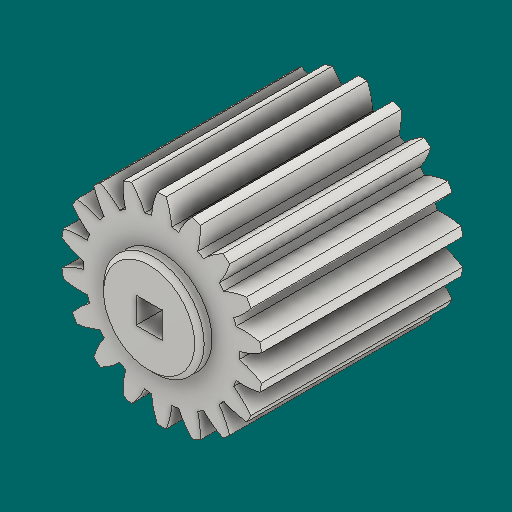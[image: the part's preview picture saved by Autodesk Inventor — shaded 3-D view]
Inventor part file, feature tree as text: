
AUTODESK INVENTOR PART (.ipt)
format: ipt  version: 2023.1 (Build 271208000, 208)  size: 353,792 bytes
history: native  units: in
note: dims shown in document units (in); Inventor stores cm internally (conversion verified against a paired STEP export)
features: other x12, sketch x5, plane x3
ambient origin geometry x8: Origin, YZ Plane, XZ Plane, XY Plane, X Axis, Y Axis, Z Axis, Center Point
bodies: Solid1 (feature_tree)
feature tree (20):
  other  "Spur Gear14_MIR.ipt"
  other  "Solid1::Spur Gear14_MIR.ipt"
  other  "TaggingFeature1"
  sketch  "Sketch1"  dims[d0=0.3937in]
  sketch  "Sketch2"  dims[d9=0.0in]
  sketch  "Sketch3"  dims[d14=0.0in]
  sketch  "Sketch4"  dims[d15=0.9in]
  sketch  "Sketch5"  dims[d16=0.0in d17=0.0in d18=0.0in d19=0.9in]
  plane  "XZ Plane_1"
  plane  "Work Plane2"
  plane  "Work Plane3"
  other  "Srf1"
  other  "Srf1::Derived"
  other  "Start plane iMate"
  other  "Distance iMate"
  other  "Position iMate"
  other  "Mesh iMate"
  other  "Axis iMate"
  other  "Mesh iMate2"
  other  "Align iMate"
